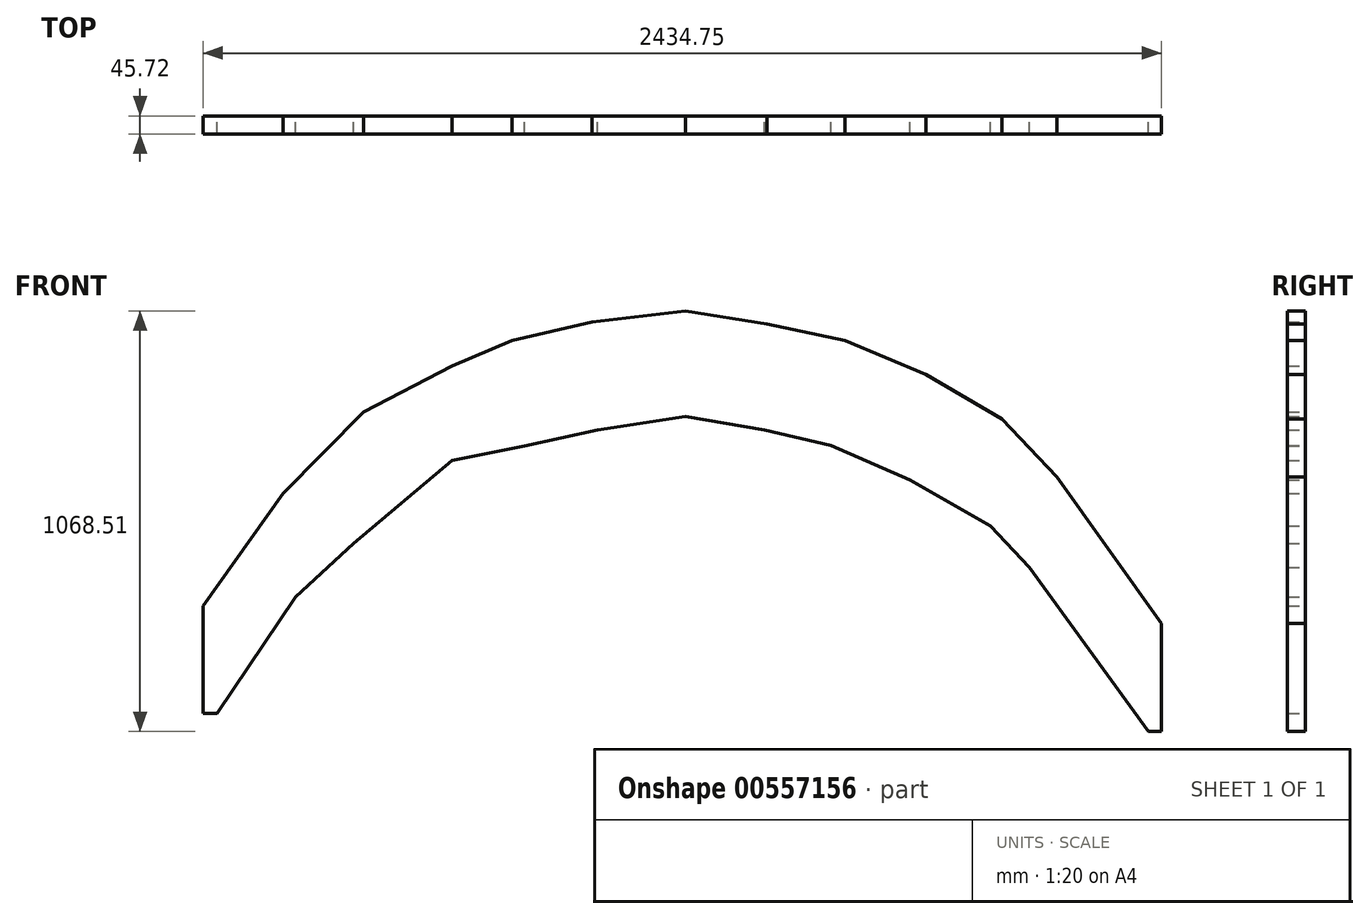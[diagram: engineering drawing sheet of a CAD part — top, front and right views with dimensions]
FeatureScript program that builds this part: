
annotation { "Feature Type Name" : "Feature", "Feature Type Description" : "" }
export const myFeature = defineFeature(function(context is Context, id is Id, definition is map)
    precondition{}
    {
        {
            var Q0;
            Q0=qCreatedBy(makeId("Front.planeOp"),FACE);
            var sketch = newSketch(context, id + "F0", { "sketchPlane" : qUnion([Q0])});
            skLineSegment(sketch, "E0", {"start": v(0, 0) * mm, "end": v(0, 273.45) * mm});
            skLineSegment(sketch, "E1", {"start": v(0, 273.45) * mm, "end": v(202.69, 558.63) * mm});
            skLineSegment(sketch, "E2", {"start": v(202.69, 558.63) * mm, "end": v(406.96, 765.28) * mm});
            skLineSegment(sketch, "E3", {"start": v(406.96, 765.28) * mm, "end": v(632.63, 883.02) * mm});
            skLineSegment(sketch, "E4", {"start": v(632.63, 883.02) * mm, "end": v(784.05, 947.84) * mm});
            skLineSegment(sketch, "E5", {"start": v(784.05, 947.84) * mm, "end": v(988.15, 994.34) * mm});
            skLineSegment(sketch, "E6", {"start": v(988.15, 994.34) * mm, "end": v(1225.19, 1022.35) * mm});
            skLineSegment(sketch, "E7", {"start": v(1225.19, 1022.35) * mm, "end": v(1432.03, 989.73) * mm});
            skLineSegment(sketch, "E8", {"start": v(1432.03, 989.73) * mm, "end": v(1630.86, 947.5) * mm});
            skLineSegment(sketch, "E9", {"start": v(1630.86, 947.5) * mm, "end": v(1836.74, 861.27) * mm});
            skLineSegment(sketch, "E10", {"start": v(1836.74, 861.27) * mm, "end": v(2029.39, 748) * mm});
            skLineSegment(sketch, "E11", {"start": v(2029.39, 748) * mm, "end": v(2168.34, 600.37) * mm});
            skLineSegment(sketch, "E12", {"start": v(2168.34, 600.37) * mm, "end": v(2434.75, 229) * mm});
            skLineSegment(sketch, "E13", {"start": v(2434.75, 229) * mm, "end": v(2434.75, -46.16) * mm});
            skLineSegment(sketch, "E14", {"start": v(2434.75, -46.16) * mm, "end": v(2401.65, -46.16) * mm});
            skLineSegment(sketch, "E15", {"start": v(2401.65, -46.16) * mm, "end": v(2099.8, 370.46) * mm});
            skLineSegment(sketch, "E16", {"start": v(2099.8, 370.46) * mm, "end": v(2000.33, 475.9) * mm});
            skLineSegment(sketch, "E17", {"start": v(2000.33, 475.9) * mm, "end": v(1796.2, 592.51) * mm});
            skLineSegment(sketch, "E18", {"start": v(1796.2, 592.51) * mm, "end": v(1594.6, 680.5) * mm});
            skLineSegment(sketch, "E19", {"start": v(1594.6, 680.5) * mm, "end": v(1426.4, 720.6) * mm});
            skLineSegment(sketch, "E20", {"start": v(1426.4, 720.6) * mm, "end": v(1225.19, 754.02) * mm});
            skLineSegment(sketch, "E21", {"start": v(1225.19, 754.02) * mm, "end": v(1002.03, 720.6) * mm});
            skLineSegment(sketch, "E22", {"start": v(1002.03, 720.6) * mm, "end": v(816.02, 679.4) * mm});
            skLineSegment(sketch, "E23", {"start": v(816.02, 679.4) * mm, "end": v(632.63, 642.64) * mm});
            skLineSegment(sketch, "E24", {"start": v(632.63, 642.64) * mm, "end": v(382.04, 432.43) * mm});
            skLineSegment(sketch, "E25", {"start": v(382.04, 432.43) * mm, "end": v(234.87, 295.4) * mm});
            skLineSegment(sketch, "E26", {"start": v(234.87, 295.4) * mm, "end": v(35.92, 0) * mm});
            skLineSegment(sketch, "E27", {"start": v(35.92, 0) * mm, "end": v(0, 0) * mm});
            skSolve(sketch);
        }
        {
            var Q0;
            Q0 = qSketchRegion(id + "F0", true);
            extrude(context, id + "F1", {"entities" : qUnion([Q0]), "depth" : 45.72 * mm, "offsetDistance" : 25.4 * mm, "symmetric" : true});
        }
    });
